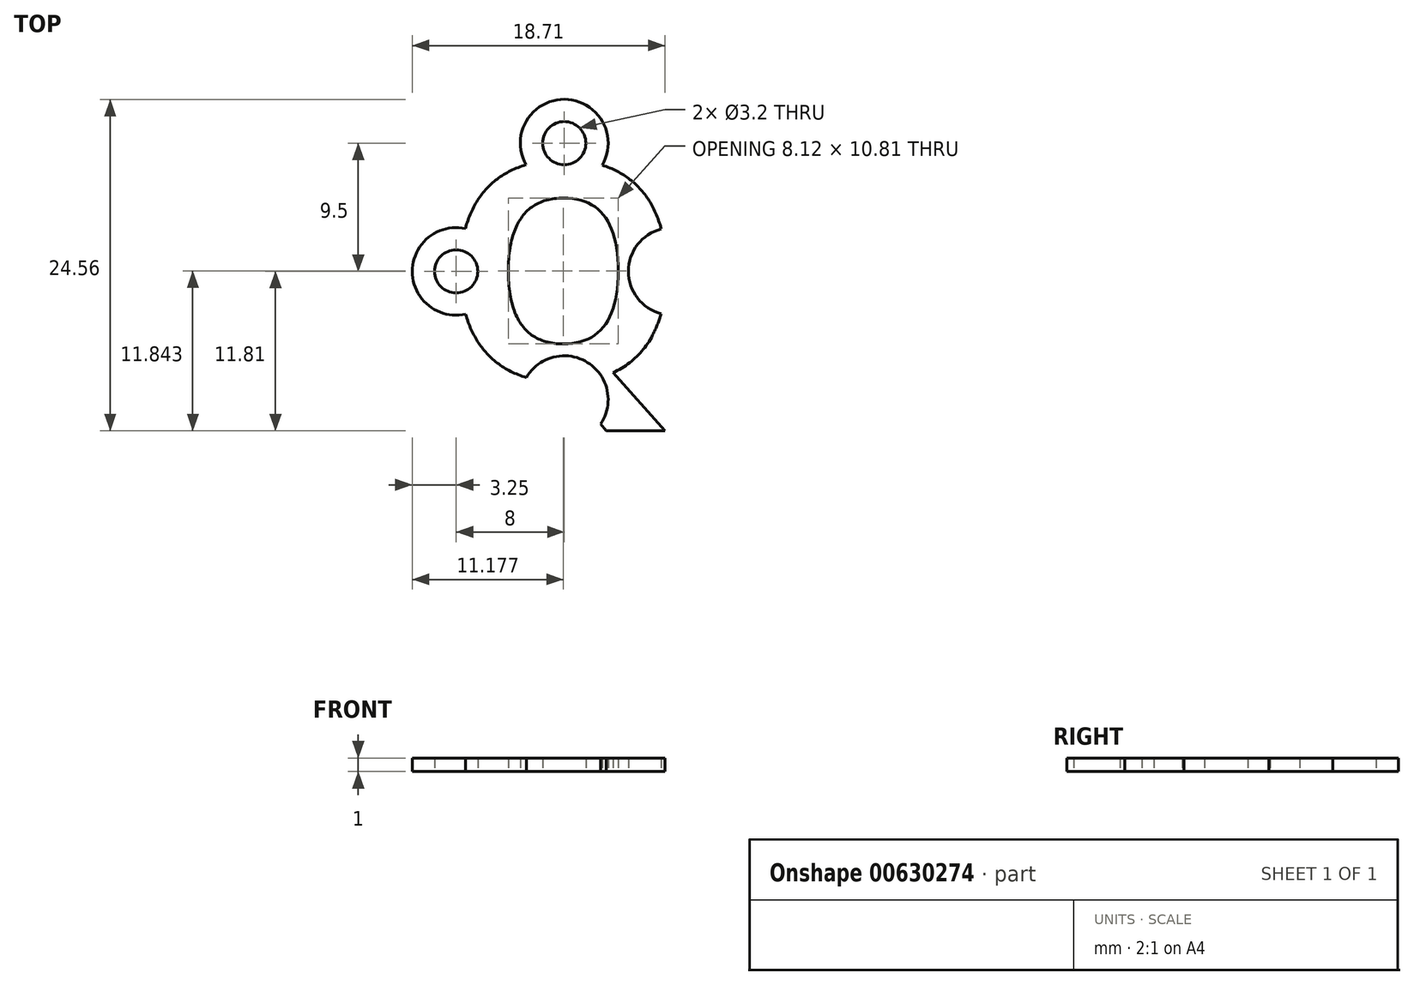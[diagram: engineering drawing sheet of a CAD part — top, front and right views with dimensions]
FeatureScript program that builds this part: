
annotation { "Feature Type Name" : "Feature", "Feature Type Description" : "" }
export const myFeature = defineFeature(function(context is Context, id is Id, definition is map)
    precondition{}
    {
        {
            var Q0;
            Q0=qCreatedBy(makeId("Top.planeOp"),FACE);
            var sketch = newSketch(context, id + "F0", { "sketchPlane" : qUnion([Q0])});
            skCircle(sketch, "E0", {"center": v(0, 0) * mm, "radius": 9.5 * mm, "construction": true});
            skCircle(sketch, "E1", {"center": v(0, 0) * mm, "radius": 8 * mm, "construction": true});
            skCircle(sketch, "E2", {"center": v(0, 9.5) * mm, "radius": 1.6 * mm});
            skCircle(sketch, "E3", {"center": v(0, 9.5) * mm, "radius": 3.25 * mm});
            skCircle(sketch, "E4.MirrorC", {"center": v(0, -9.5) * mm, "radius": 3.25 * mm});
            skCircle(sketch, "E5.MirrorC", {"center": v(0, -9.5) * mm, "radius": 1.6 * mm});
            skCircle(sketch, "E6", {"center": v(-8, 0) * mm, "radius": 1.6 * mm});
            skCircle(sketch, "E7", {"center": v(-8, 0) * mm, "radius": 3.25 * mm});
            skCircle(sketch, "E8.MirrorC", {"center": v(8, 0) * mm, "radius": 3.25 * mm});
            skCircle(sketch, "E9.MirrorC", {"center": v(8, 0) * mm, "radius": 1.6 * mm});
            skText(sketch, "E10", { "text": "Q", "fontName": "OpenSans-Bold.ttf"});
            const initialGuessF0  = {"E10": [-0.009, -0.008, 1, 0, 0.01615]};
            skSetInitialGuess(sketch, initialGuessF0);
            skSolve(sketch);
        }
        {
            var Q0;
            {var subQ8=sQuery(id+"F0.wireOp",EDGE,"E10.sketch_text.stroke-1");Q0=makeQuery(id+"F0.imprint","IMPRINT",FACE,{"disambiguationData":[TD([[makeQuery(id+"F0.imprint","IMPRINT",EDGE,{"derivedFrom":subQ8}),-1.0]])]});}
            var Q1;
            {var subQ0=sQuery(id+"F0.wireOp",EDGE,"E10.sketch_text.stroke-7");var subQ1=sQuery(id+"F0.wireOp",EDGE,"E6");var subQ2=makeQuery(id+"F0.imprint","INTERSECT",VERTEX,{"derivedFrom":[subQ1,subQ0]});Q1=makeQuery(id+"F0.imprint","IMPRINT",FACE,{"disambiguationData":[TD([[makeQuery(id+"F0.imprint","IMPRINT",EDGE,{"disambiguationData":[TD([[subQ2,-1.0]])],"derivedFrom":subQ1}),-1.0]])]});}
            var Q2;
            {var subQ0=sQuery(id+"F0.wireOp",EDGE,"E10.sketch_text.stroke-7");var subQ1=sQuery(id+"F0.wireOp",EDGE,"E6");var subQ2=makeQuery(id+"F0.imprint","INTERSECT",VERTEX,{"derivedFrom":[subQ1,subQ0]});Q2=makeQuery(id+"F0.imprint","IMPRINT",FACE,{"disambiguationData":[TD([[makeQuery(id+"F0.imprint","IMPRINT",EDGE,{"disambiguationData":[TD([[subQ2,1.0]])],"derivedFrom":subQ1}),-1.0]])]});}
            var Q3;
            {var subQ0=sQuery(id+"F0.wireOp",EDGE,"E10.sketch_text.stroke-9");var subQ1=sQuery(id+"F0.wireOp",EDGE,"E2");var subQ2=makeQuery(id+"F0.imprint","INTERSECT",VERTEX,{"derivedFrom":[subQ1,subQ0]});Q3=makeQuery(id+"F0.imprint","IMPRINT",FACE,{"disambiguationData":[TD([[makeQuery(id+"F0.imprint","IMPRINT",EDGE,{"disambiguationData":[TD([[subQ2,1.0]])],"derivedFrom":subQ1}),-1.0]])]});}
            var Q4;
            {var subQ0=sQuery(id+"F0.wireOp",EDGE,"E10.sketch_text.stroke-9");var subQ1=sQuery(id+"F0.wireOp",EDGE,"E2");var subQ2=makeQuery(id+"F0.imprint","INTERSECT",VERTEX,{"derivedFrom":[subQ1,subQ0]});Q4=makeQuery(id+"F0.imprint","IMPRINT",FACE,{"disambiguationData":[TD([[makeQuery(id+"F0.imprint","IMPRINT",EDGE,{"disambiguationData":[TD([[subQ2,-1.0]])],"derivedFrom":subQ1}),-1.0]])]});}
            var Q5;
            {var subQ0=sQuery(id+"F0.wireOp",EDGE,"E10.sketch_text.stroke-0");var subQ1=sQuery(id+"F0.wireOp",EDGE,"E8.MirrorC");var subQ2=makeQuery(id+"F0.imprint","INTERSECT",VERTEX,{"derivedFrom":[subQ1,subQ0]});Q5=makeQuery(id+"F0.imprint","IMPRINT",FACE,{"disambiguationData":[TD([[makeQuery(id+"F0.imprint","IMPRINT",EDGE,{"disambiguationData":[TD([[subQ2,1.0]])],"derivedFrom":subQ1}),-1.0]])]});}
            var Q6;
            {var subQ0=sQuery(id+"F0.wireOp",EDGE,"E10.sketch_text.stroke-0");var subQ1=sQuery(id+"F0.wireOp",EDGE,"E8.MirrorC");var subQ2=makeQuery(id+"F0.imprint","INTERSECT",VERTEX,{"derivedFrom":[subQ1,subQ0]});Q6=makeQuery(id+"F0.imprint","IMPRINT",FACE,{"disambiguationData":[TD([[makeQuery(id+"F0.imprint","IMPRINT",EDGE,{"disambiguationData":[TD([[subQ2,-1.0]])],"derivedFrom":subQ1}),-1.0]])]});}
            var Q7;
            {var subQ0=sQuery(id+"F0.wireOp",EDGE,"E10.sketch_text.stroke-4");var subQ1=sQuery(id+"F0.wireOp",EDGE,"E4.MirrorC");var subQ2=makeQuery(id+"F0.imprint","INTERSECT",VERTEX,{"derivedFrom":[subQ1,subQ0]});Q7=makeQuery(id+"F0.imprint","IMPRINT",FACE,{"disambiguationData":[TD([[makeQuery(id+"F0.imprint","IMPRINT",EDGE,{"disambiguationData":[TD([[subQ2,1.0]])],"derivedFrom":subQ1}),-1.0]])]});}
            var Q8;
            {var subQ0=sQuery(id+"F0.wireOp",EDGE,"E10.sketch_text.stroke-4");var subQ1=sQuery(id+"F0.wireOp",EDGE,"E4.MirrorC");var subQ2=makeQuery(id+"F0.imprint","INTERSECT",VERTEX,{"derivedFrom":[subQ1,subQ0]});Q8=makeQuery(id+"F0.imprint","IMPRINT",FACE,{"disambiguationData":[TD([[makeQuery(id+"F0.imprint","IMPRINT",EDGE,{"disambiguationData":[TD([[subQ2,-1.0]])],"derivedFrom":subQ1}),-1.0]])]});}
            extrude(context, id + "F1", {"entities" : qUnion([Q0, Q1, Q2, Q3, Q4, Q5, Q6, Q7, Q8]), "depth" : 1 * mm, "offsetDistance" : 25 * mm});
        }
    });
